# Revit family: Backwater-Valve_Zurn-Z1088
name_source: partatom
category: Plumbing Fixtures
units: mm (PartAtom-declared; Revit-internal decimal feet)

## family parameters
Always vertical = Yes
Cut with Voids When Loaded = No
Maintain Annotation Orientation = No
OmniClass Number = 23.45.55.21
OmniClass Title = Drains (Wastes)
Part Type = Normal
Room Calculation Point = No
Round Connector Dimension = Use Radius
Shared = No
Work Plane-Based = No

## types (6) — shared parameters
Assembly Code = D2040100
CW Connection = No
Default Elevation = 20 "
Description = BACKWATER VALVE GATE TYPE
HW Connection = No
Main Material = Iron - Zurn - Cast - Painted - Blue
Manufacturer = Zurn Water, LLC
Manufacturer Brand = Zurn
Model = Z1088
Modified Date = 02/20/2026
Product Documentation Link = https://files.zurn.com
Product Installation Sheet URL = https://files.zurn.com
Product Page URL = https://www.zurn.com
Product data url = https://www.bimobject.com
URL = http://zurn.com
Vent Connection = No
WFU = 1
Waste Connection = Yes
zero-valued in all types: CWFU, HWFU

## per-type parameters (varying)
| type | Approx. Weight (Lbs) | Connector Radius | DIM_C | DIM_C-0.25 | DIM_C_For Masking Region | DIM_E | DIM_Length_For Masking Region | DIM_M | DIM_M/2 | Hub Outer Diamter | Hub-Left | Hub-Right | Length (G) | Pipe Size_A Inside Diameter | Pipe Size_A Nominal Diameter | Pipe Size_A Outer Diameter | Top Slot Inside Diamter | Top Slot Outer Diamter | Width |
| Z1088_4 HB X 4 HB | 80.000 lb | 2 " | 8 " | 7.75 " | 8.25 " | 12 " | 3 " | 15.75 " | 7.875 " | 5 " | Yes | Yes | 14 " | 4.026 " | 4 " | 4.5 " | 7 " | 7.25 " | 5.5 " |
| Z1088_6 HB X 6 HB | 120.000 lb | 3 " | 10.5 " | 10.25 " | 10.75 " | 14.5 " | 3.188 " | 19 " | 9.5 " | 7.126 " | Yes | Yes | 16 " | 6.065 " | 6 " | 6.625 " | 9.5 " | 9.75 " | 8 " |
| Z1088_4 HB X 4 NH | 80.000 lb | 2 " | 8 " | 7.75 " | 8.25 " | 12 " | 5 " | 15.75 " | 7.875 " | 5 " | Yes | No | 18 " | 4.026 " | 4 " | 4.5 " | 7 " | 7.25 " | 5.5 " |
| Z1088_6 HB X 6 NH | 120.000 lb | 3 " | 10.5 " | 10.25 " | 10.75 " | 14.5 " | 5.188 " | 19 " | 9.5 " | 7.126 " | Yes | No | 20 " | 6.065 " | 6 " | 6.625 " | 9.5 " | 9.75 " | 8 " |
| Z1088_4 NH X 4 NH | 80.000 lb | 2 " | 8 " | 7.75 " | 8.25 " | 12 " | 5 " | 15.75 " | 7.875 " | 5 " | No | No | 18 " | 4.026 " | 4 " | 4.5 " | 7 " | 7.25 " | 5.5 " |
| Z1088_6 NH X 6 NH | 120.000 lb | 3 " | 10.5 " | 10.25 " | 10.75 " | 14.5 " | 3.188 " | 19 " | 9.5 " | 7.126 " | No | No | 16 " | 6.065 " | 6 " | 6.625 " | 9.5 " | 9.75 " | 8 " |

## geometry (parser evidence)
native form markers: Sweep x3
no freeform markers — native parametric forms only
